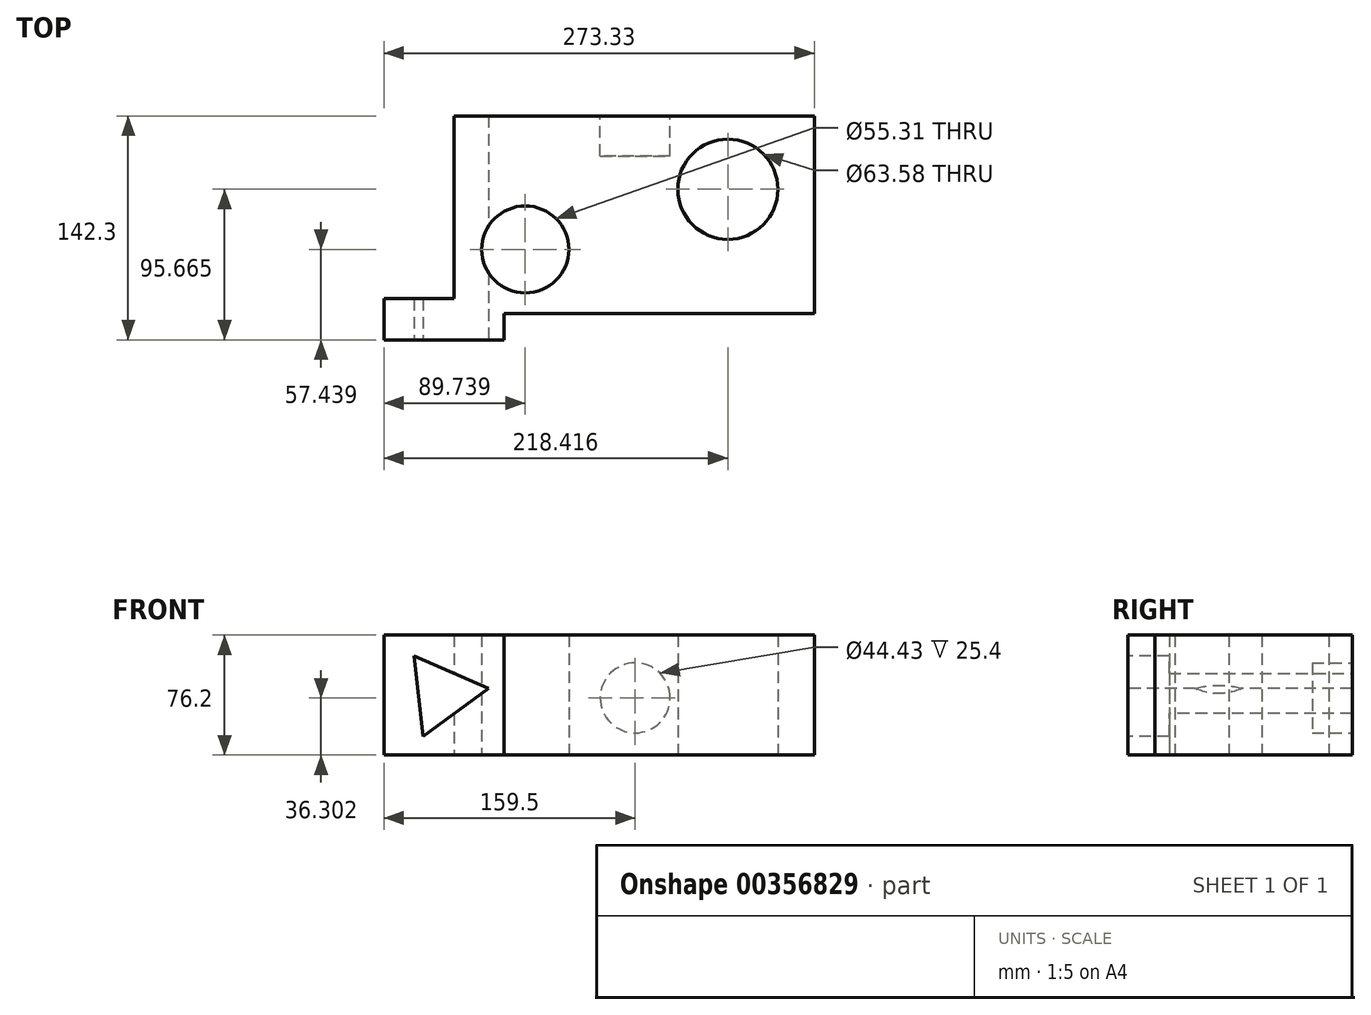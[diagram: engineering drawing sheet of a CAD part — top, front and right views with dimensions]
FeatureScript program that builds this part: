
annotation { "Feature Type Name" : "Feature", "Feature Type Description" : "" }
export const myFeature = defineFeature(function(context is Context, id is Id, definition is map)
    precondition{}
    {
        {
            var Q0;
            Q0=qCreatedBy(makeId("Top.planeOp"),FACE);
            var sketch = newSketch(context, id + "F0", { "sketchPlane" : qUnion([Q0])});
            skLineSegment(sketch, "E0.bottom", {"start": v(-111.42, 64.56) * mm, "end": v(117.25, 64.56) * mm});
            skLineSegment(sketch, "E0.top", {"start": v(-79.9, -60.9) * mm, "end": v(117.25, -60.9) * mm});
            skLineSegment(sketch, "E0.left", {"start": v(-111.42, 64.56) * mm, "end": v(-111.42, -51.63) * mm});
            skLineSegment(sketch, "E0.right", {"start": v(117.25, 64.56) * mm, "end": v(117.25, -60.9) * mm});
            skCircle(sketch, "E1", {"center": v(-66.34, -20.3) * mm, "radius": 27.65 * mm});
            skCircle(sketch, "E2", {"center": v(62.34, 17.93) * mm, "radius": 31.79 * mm});
            skLineSegment(sketch, "E3.bottom", {"start": v(-156.08, -51.63) * mm, "end": v(-111.42, -51.63) * mm});
            skLineSegment(sketch, "E3.top", {"start": v(-156.08, -77.74) * mm, "end": v(-79.9, -77.74) * mm});
            skLineSegment(sketch, "E3.left", {"start": v(-156.08, -51.63) * mm, "end": v(-156.08, -77.74) * mm});
            skLineSegment(sketch, "E3.right", {"start": v(-79.9, -60.9) * mm, "end": v(-79.9, -77.74) * mm});
            skLineSegment(sketch, "E4", {"start": v(-161.2, 47.18) * mm, "end": v(-116.8, 82.19) * mm, "construction": true});
            skSolve(sketch);
        }
        {
            var Q0;
            Q0 = qSketchRegion(id + "F0", true);
            extrude(context, id + "F1", {"entities" : qUnion([Q0]), "depth" : 76.2 * mm});
        }
        {
            var Q0;
            Q0=makeQuery(id+"F1.opExtrude","SWEPT_FACE",FACE,{"disambiguationData":[OSD([sQuery(id+"F0.wireOp",EDGE,"E3.top")])]});
            var sketch = newSketch(context, id + "F2", { "sketchPlane" : qUnion([Q0])});
            skCircle(sketch, "E5.cCircle", {"center": v(-119.3, 39.06) * mm, "radius": 14.93 * mm, "construction": true});
            skLineSegment(sketch, "E5.0", {"start": v(-89.6, 42.35) * mm, "end": v(-131.28, 11.7) * mm});
            skLineSegment(sketch, "E5.1", {"start": v(-131.28, 11.7) * mm, "end": v(-136.99, 63.12) * mm});
            skLineSegment(sketch, "E5.2", {"start": v(-136.99, 63.12) * mm, "end": v(-89.6, 42.35) * mm});
            skPoint(sketch, "E5.0.midPoint", {"position": v(-110.44, 27.03) * mm});
            skSolve(sketch);
        }
        {
            var Q0;
            Q0=makeQuery(id+"F1.opExtrude","SWEPT_FACE",FACE,{"disambiguationData":[OSD([sQuery(id+"F0.wireOp",EDGE,"E0.bottom")])]});
            var sketch = newSketch(context, id + "F3", { "sketchPlane" : qUnion([Q0])});
            skCircle(sketch, "E6", {"center": v(-3.42, 36.3) * mm, "radius": 22.21 * mm});
            skSolve(sketch);
        }
        {
            var Q0;
            Q0 = qSketchRegion(id + "F3", true);
            extrude(context, id + "F4", {"entities" : qUnion([Q0]), "operationType" : NewBodyOperationType.REMOVE, "oppositeDirection" : true, "depth" : 25.4 * mm});
        }
        {
            var Q0;
            Q0=makeQuery(id+"F2.imprint","IMPRINT",FACE,{"disambiguationData":[TD([[makeQuery(id+"F2.imprint","IMPRINT",EDGE,{"derivedFrom":sQuery(id+"F2.wireOp",EDGE,"E5.0")}),-1.0]])]});
            extrude(context, id + "F5", {"entities" : qUnion([Q0]), "operationType" : NewBodyOperationType.REMOVE, "oppositeDirection" : true, "depth" : 157.73 * mm});
        }
    });
